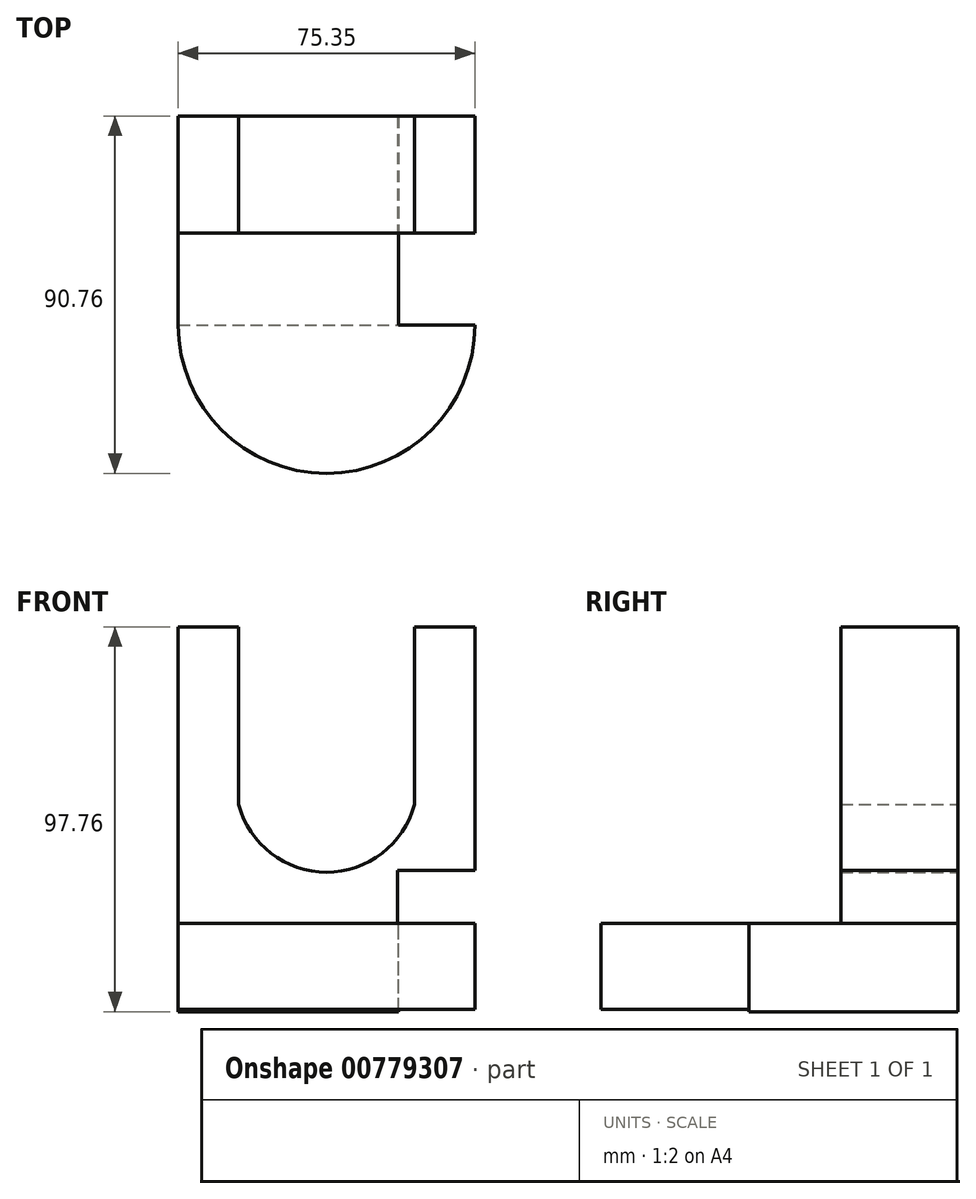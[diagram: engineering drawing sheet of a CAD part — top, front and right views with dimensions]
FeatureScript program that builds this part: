
annotation { "Feature Type Name" : "Feature", "Feature Type Description" : "" }
export const myFeature = defineFeature(function(context is Context, id is Id, definition is map)
    precondition{}
    {
        {
            var Q0;
            Q0=qCreatedBy(makeId("Front.planeOp"),FACE);
            var sketch = newSketch(context, id + "F0", { "sketchPlane" : qUnion([Q0])});
            skLineSegment(sketch, "E0.bottom", {"start": v(-75.35, 75.35) * mm, "end": v(-60, 75.35) * mm});
            skLineSegment(sketch, "E0.top", {"start": v(-75.35, -22.4) * mm, "end": v(0, -22.4) * mm});
            skLineSegment(sketch, "E0.left", {"start": v(-75.35, 75.35) * mm, "end": v(-75.35, -22.4) * mm});
            skLineSegment(sketch, "E0.right", {"start": v(0, 75.35) * mm, "end": v(0, -22.4) * mm});
            skLineSegment(sketch, "E1", {"start": v(-60, 75.35) * mm, "end": v(-60, 30.23) * mm});
            skLineSegment(sketch, "E2", {"start": v(-15.34, 30.23) * mm, "end": v(-15.34, 75.35) * mm});
            skLineSegment(sketch, "E3.trimOffspring", {"start": v(-15.34, 75.35) * mm, "end": v(0, 75.35) * mm});
            skLineSegment(sketch, "E4.bottom", {"start": v(-75.35, 0) * mm, "end": v(0, 0) * mm});
            skLineSegment(sketch, "E4.left", {"start": v(-75.35, 0) * mm, "end": v(-75.35, -22.4) * mm});
            skLineSegment(sketch, "E4.right", {"start": v(0, 0) * mm, "end": v(0, -22.4) * mm});
            skArc(sketch, "E5", {"start": v(-60, 30.23) * mm, "mid": v(-37.67, 13.03) * mm, "end": v(-15.34, 30.23) * mm});
            skSolve(sketch);
        }
        {
            var Q0;
            {var subQ4=sQuery(id+"F0.wireOp",EDGE,"E0.bottom");Q0=makeQuery(id+"F0.imprint","IMPRINT",FACE,{"disambiguationData":[TD([[makeQuery(id+"F0.imprint","IMPRINT",EDGE,{"derivedFrom":subQ4}),-1.0]])]});}
            extrude(context, id + "F1", {"entities" : qUnion([Q0]), "depth" : 29.72 * mm, "offsetDistance" : 25.4 * mm});
        }
        {
            var Q0;
            {var subQ0=sQuery(id+"F0.wireOp",EDGE,"E0.top");Q0=makeQuery(id+"F0.imprint","IMPRINT",FACE,{"disambiguationData":[TD([[makeQuery(id+"F0.imprint","IMPRINT",EDGE,{"derivedFrom":subQ0}),1.0]])]});}
            extrude(context, id + "F2", {"entities" : qUnion([Q0]), "operationType" : NewBodyOperationType.ADD, "depth" : 53.1 * mm, "offsetDistance" : 25.4 * mm});
        }
        {
            var Q0;
            Q0=makeQuery(id+"F2.opExtrude","SWEPT_FACE",FACE,{"disambiguationData":[OSD([sQuery(id+"F0.wireOp",EDGE,"E4.bottom")])]});
            var sketch = newSketch(context, id + "F3", { "sketchPlane" : qUnion([Q0])});
            skArc(sketch, "E6", {"start": v(-75.35, -53.09) * mm, "mid": v(-37.67, -90.76) * mm, "end": v(0, -53.09) * mm});
            skSolve(sketch);
        }
        {
            var Q0;
            Q0=makeQuery(id+"F3.imprint","IMPRINT",FACE,{"disambiguationData":[TD([[makeQuery(id+"F3.imprint","IMPRINT",EDGE,{"derivedFrom":sQuery(id+"F3.wireOp",EDGE,"E6")}),1.0]])]});
            extrude(context, id + "F4", {"entities" : qUnion([Q0]), "operationType" : NewBodyOperationType.ADD, "oppositeDirection" : true, "depth" : 21.84 * mm, "offsetDistance" : 25.4 * mm});
        }
        {
            var Q0;
            {var subQ0=sQuery(id+"F0.wireOp",EDGE,"E4.bottom");Q0=makeQuery(id+"F4.boolean.opBoolean","MERGE",FACE,{"derivedFrom":[makeQuery(id+"F2.opExtrude","SWEPT_FACE",FACE,{"disambiguationData":[OSD([subQ0])]}),makeQuery(id+"F4.opExtrude","CAP_FACE",FACE,{"disambiguationData":[OSD([subQ0,sQuery(id+"F3.wireOp",EDGE,"E6")])],"isStart":true})]});}
            var sketch = newSketch(context, id + "F5", { "sketchPlane" : qUnion([Q0])});
            skLineSegment(sketch, "E7.bottom", {"start": v(-19.4, -29.72) * mm, "end": v(0, -29.72) * mm});
            skLineSegment(sketch, "E7.top", {"start": v(-19.4, -53.09) * mm, "end": v(0, -53.09) * mm});
            skLineSegment(sketch, "E7.left", {"start": v(-19.4, -29.72) * mm, "end": v(-19.4, -53.09) * mm});
            skLineSegment(sketch, "E7.right", {"start": v(0, -29.72) * mm, "end": v(0, -53.09) * mm});
            skSolve(sketch);
        }
        {
            var Q0;
            Q0=makeQuery(id+"F5.imprint","IMPRINT",FACE,{"disambiguationData":[TD([[makeQuery(id+"F5.imprint","IMPRINT",EDGE,{"derivedFrom":sQuery(id+"F5.wireOp",EDGE,"E7.bottom")}),-1.0]])]});
            extrude(context, id + "F6", {"entities" : qUnion([Q0]), "operationType" : NewBodyOperationType.REMOVE, "endBound" : BoundingType.THROUGH_ALL, "oppositeDirection" : true, "depth" : 24.64 * mm, "offsetDistance" : 25.4 * mm});
        }
        {
            var Q0;
            Q0=makeQuery(id+"F6.boolean.opBoolean","MERGE",FACE,{"derivedFrom":[makeQuery(id+"F1.opExtrude","CAP_FACE",FACE,{"disambiguationData":[OSD([sQuery(id+"F0.wireOp",EDGE,"E0.bottom"),sQuery(id+"F0.wireOp",EDGE,"E0.left"),sQuery(id+"F0.wireOp",EDGE,"E0.right"),sQuery(id+"F0.wireOp",EDGE,"E1"),sQuery(id+"F0.wireOp",EDGE,"E2"),sQuery(id+"F0.wireOp",EDGE,"E3.trimOffspring"),sQuery(id+"F0.wireOp",EDGE,"E4.bottom"),sQuery(id+"F0.wireOp",EDGE,"E5")])],"isStart":false})],"fromTools":[makeQuery(id+"F6.opExtrude","SWEPT_FACE",FACE,{"disambiguationData":[OSD([sQuery(id+"F5.wireOp",EDGE,"E7.bottom")])]})]});
            var sketch = newSketch(context, id + "F7", { "sketchPlane" : qUnion([Q0])});
            skLineSegment(sketch, "E8.bottom", {"start": v(-19.7, 13.45) * mm, "end": v(0, 13.45) * mm});
            skLineSegment(sketch, "E8.top", {"start": v(-19.7, -22.4) * mm, "end": v(0, -22.4) * mm});
            skLineSegment(sketch, "E8.left", {"start": v(-19.7, 13.45) * mm, "end": v(-19.7, -22.4) * mm});
            skLineSegment(sketch, "E8.right", {"start": v(0, 13.45) * mm, "end": v(0, -22.4) * mm});
            skSolve(sketch);
        }
        {
            var Q0;
            {var subQ1=sQuery(id+"F7.wireOp",EDGE,"E8.bottom");Q0=makeQuery(id+"F7.imprint","IMPRINT",FACE,{"disambiguationData":[TD([[makeQuery(id+"F7.imprint","IMPRINT",EDGE,{"derivedFrom":subQ1}),-1.0]])]});}
            extrude(context, id + "F8", {"entities" : qUnion([Q0]), "operationType" : NewBodyOperationType.REMOVE, "endBound" : BoundingType.THROUGH_ALL, "oppositeDirection" : true, "depth" : 31.5 * mm, "offsetDistance" : 25.4 * mm});
        }
    });
